# Revit family: Emergency_Valve-Tepid-SV160
name_source: partatom
category: Pipe Accessories
revit_build: Autodesk Revit 2016 (Build: 20150220_1215(x64)
units: mm (PartAtom-declared; Revit-internal decimal feet)

## family parameters
Always vertical = Yes
Cut with Voids When Loaded = No
OmniClass Number = 23.65.55.14.17
OmniClass Title = Adjusting/Controlling Valves for Liquid Services
Part Type = Valve - Breaks Into
Round Connector Dimension = Use Radius
Shared = No
Work Plane-Based = No

## types (20) — shared parameters
BC = Yes
Body Length = 0' - 11"
C Length = 0' - 3 3/32"
CC = Yes
Cabinet Exposed = No
Cabinet Recessed = Yes
Description = Emergency Mixing Valve
Dimension Disclaimer = Dimensions are ±0.50”. Design and specifications are subject to change without notice.
Flow = 4 GPM
Flow Maximum = 72 GPM
K Coefficient = 3.5
Manufacturer = Stingray Systems
Nominal Diameter = 1"
Nominal Radius = 1"
Option = 3
Product Documentation Link = https://www.tepid.com
Product Name = ThermostaticMixing Valve
Product Page URL = https://www.tepid.com
TC = No
Temp. Range = 70°F-90°F
URL = https://www.tepid.com
Version = 2016-v1.0a

## per-type parameters (varying)
| type | Cabinet Material | Model | Valve Material |
| PIPED VALVE-TOP, ROUGH BRASS | Paint - Stingray - Baked White Enamel | SV-160 PIPED VALVE-TOP, ROUGH BRASS | Metal - Stingray - Rough Bronze |
| PIPED VALVE-TOP, CHROME PLATED | Paint - Stingray - Baked White Enamel | SV-160 PIPED VALVE-TOP, CHROME PLATED | Metal - Stingray - Chrome Plated |
| PIPED VALVE-BOT, ROUGH BRASS | Paint - Stingray - Baked White Enamel | SV-160 PIPED VALVE-BOT, ROUGH BRASS | Metal - Stingray - Rough Bronze |
| PIPED VALVE-BOT, CHROME PLATED | Paint - Stingray - Baked White Enamel | SV-160 PIPED VALVE-BOT, CHROME PLATED | Metal - Stingray - Chrome Plated |
| PIPED VALVE-TOP, ROUGH BRASS, EXP CAB BWE - CABINET EXPOSED - BAKED WHITE ENAMEL | Paint - Stingray - Baked White Enamel | SV-160 PIPED VALVE-TOP, ROUGH BRASS, EXP CAB BWE - CABINET EXPOSED - BAKED WHITE ENAMEL | Metal - Stingray - Rough Bronze |
| PIPED VALVE-TOP, CHROME PLATED, EXP CAB BWE - CABINET EXPOSED - BAKED WHITE ENAMEL | Paint - Stingray - Baked White Enamel | SV-160 PIPED VALVE-TOP, CHROME PLATED, EXP CAB BWE - CABINET EXPOSED - BAKED WHITE ENAMEL | Metal - Stingray - Chrome Plated |
| PIPED VALVE-BOT, ROUGH BRASS, EXP CAB BWE - CABINET EXPOSED - BAKED WHITE ENAMEL | Paint - Stingray - Baked White Enamel | SV-160 PIPED VALVE-BOT, ROUGH BRASS, EXP CAB BWE - CABINET EXPOSED - BAKED WHITE ENAMEL | Metal - Stingray - Rough Bronze |
| PIPED VALVE-BOT, CHROME PLATED, EXP CAB BWE - CABINET EXPOSED - BAKED WHITE ENAMEL | Paint - Stingray - Baked White Enamel | SV-160 PIPED VALVE-BOT, CHROME PLATED, EXP CAB BWE - CABINET EXPOSED - BAKED WHITE ENAMEL | Metal - Stingray - Chrome Plated |
| PIPED VALVE-TOP, ROUGH BRASS, EXP CAB SS - CABINET EXPOSED - STAINLESS STEEL | Metal - Stingray - Stainless Steel SS | SV-160 PIPED VALVE-TOP, ROUGH BRASS, EXP CAB SS - CABINET EXPOSED - STAINLESS STEEL | Metal - Stingray - Rough Bronze |
| PIPED VALVE-TOP, CHROME PLATED, EXP CAB SS - CABINET EXPOSED - STAINLESS STEEL | Metal - Stingray - Stainless Steel SS | SV-160 PIPED VALVE-TOP, CHROME PLATED, EXP CAB SS - CABINET EXPOSED - STAINLESS STEEL | Metal - Stingray - Chrome Plated |
| PIPED VALVE-BOT, ROUGH BRASS, EXP CAB SS - CABINET EXPOSED - STAINLESS STEEL | Metal - Stingray - Stainless Steel SS | SV-160 PIPED VALVE-BOT, ROUGH BRASS, EXP CAB SS - CABINET EXPOSED - STAINLESS STEEL | Metal - Stingray - Rough Bronze |
| PIPED VALVE-BOT, CHROME PLATED, EXP CAB SS - CABINET EXPOSED - STAINLESS STEEL | Metal - Stingray - Stainless Steel SS | SV-160 PIPED VALVE-BOT, CHROME PLATED, EXP CAB SS - CABINET EXPOSED - STAINLESS STEEL | Metal - Stingray - Chrome Plated |
| PIPED VALVE-TOP, ROUGH BRASS, REC CAB BWE - CABINET RECESSED - BAKED WHITE ENAMEL | Paint - Stingray - Baked White Enamel | SV-160 PIPED VALVE-TOP, ROUGH BRASS, REC CAB BWE - CABINET RECESSED - BAKED WHITE ENAMEL | Metal - Stingray - Rough Bronze |
| PIPED VALVE-TOP, CHROME PLATED, REC CAB BWE - CABINET RECESSED - BAKED WHITE ENAMEL | Paint - Stingray - Baked White Enamel | SV-160 PIPED VALVE-TOP, CHROME PLATED, REC CAB BWE - CABINET RECESSED - BAKED WHITE ENAMEL | Metal - Stingray - Chrome Plated |
| PIPED VALVE-BOT, ROUGH BRASS, REC CAB BWE - CABINET RECESSED - BAKED WHITE ENAMEL | Paint - Stingray - Baked White Enamel | SV-160 PIPED VALVE-BOT, ROUGH BRASS, REC CAB BWE - CABINET RECESSED - BAKED WHITE ENAMEL | Metal - Stingray - Rough Bronze |
| PIPED VALVE-BOT, CHROME PLATED, REC CAB BWE - CABINET RECESSED - BAKED WHITE ENAMEL | Paint - Stingray - Baked White Enamel | SV-160 PIPED VALVE-BOT, CHROME PLATED, REC CAB BWE - CABINET RECESSED - BAKED WHITE ENAMEL | Metal - Stingray - Chrome Plated |
| PIPED VALVE-TOP, ROUGH BRASS, REC CAB SS - CABINET RECESSED - STAINLESS STEEL | Metal - Stingray - Stainless Steel SS | SV-160 PIPED VALVE-TOP, ROUGH BRASS, REC CAB SS - CABINET RECESSED - STAINLESS STEEL | Metal - Stingray - Rough Bronze |
| PIPED VALVE-TOP, CHROME PLATED, REC CAB SS - CABINET RECESSED - STAINLESS STEEL | Metal - Stingray - Stainless Steel SS | SV-160 PIPED VALVE-TOP, CHROME PLATED, REC CAB SS - CABINET RECESSED - STAINLESS STEEL | Metal - Stingray - Chrome Plated |
| PIPED VALVE-BOT, ROUGH BRASS, REC CAB SS - CABINET RECESSED - STAINLESS STEEL | Metal - Stingray - Stainless Steel SS | SV-160 PIPED VALVE-BOT, ROUGH BRASS, REC CAB SS - CABINET RECESSED - STAINLESS STEEL | Metal - Stingray - Rough Bronze |
| PIPED VALVE-BOT, CHROME PLATED, REC CAB SS - CABINET RECESSED - STAINLESS STEEL | Metal - Stingray - Stainless Steel SS | SV-160 PIPED VALVE-BOT, CHROME PLATED, REC CAB SS - CABINET RECESSED - STAINLESS STEEL | Metal - Stingray - Chrome Plated |

## geometry (parser evidence)
native form markers: Sweep x1
no freeform markers — native parametric forms only
